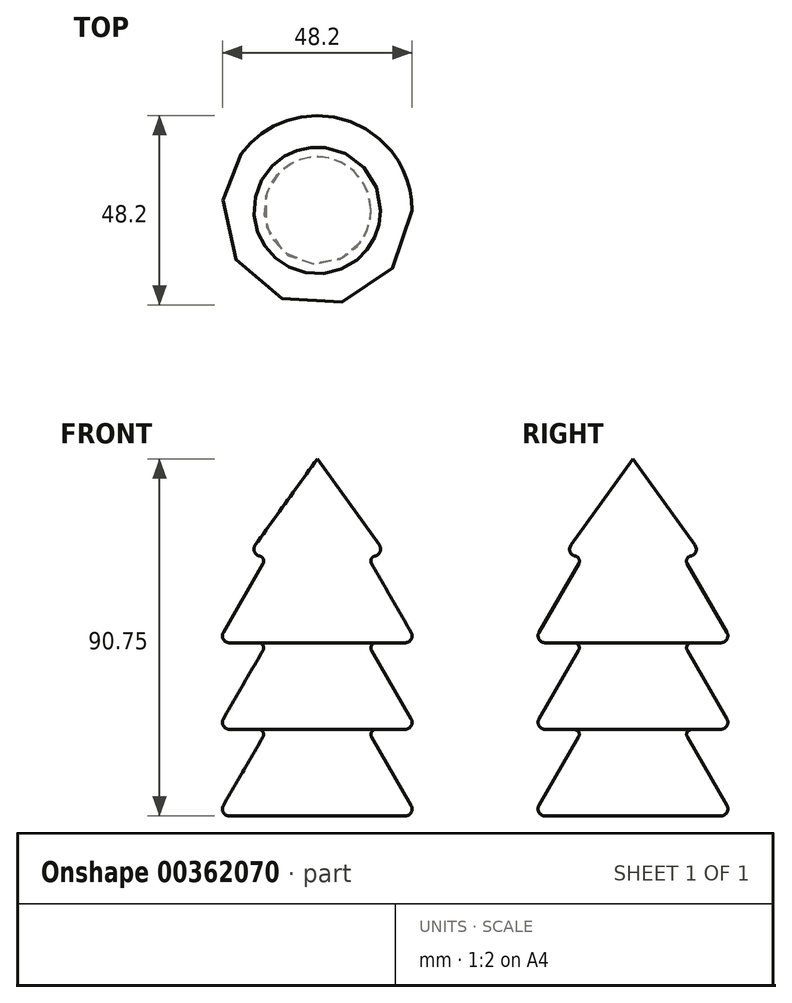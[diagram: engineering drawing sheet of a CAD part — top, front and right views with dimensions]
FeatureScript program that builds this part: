
annotation { "Feature Type Name" : "Feature", "Feature Type Description" : "" }
export const myFeature = defineFeature(function(context is Context, id is Id, definition is map)
    precondition{}
    {
        {
            var Q0;
            Q0=qCreatedBy(makeId("Front.planeOp"),FACE);
            var sketch = newSketch(context, id + "F0", { "sketchPlane" : qUnion([Q0])});
            skLineSegment(sketch, "E0", {"start": v(0, -34.34) * mm, "end": v(-25.4, -34.34) * mm});
            skLineSegment(sketch, "E1", {"start": v(-25.4, -34.34) * mm, "end": v(-12.7, -12.34) * mm});
            skLineSegment(sketch, "E2", {"start": v(-12.7, -12.34) * mm, "end": v(-25.4, -12.34) * mm});
            skLineSegment(sketch, "E3", {"start": v(-25.4, -12.34) * mm, "end": v(-12.7, 9.65) * mm});
            skLineSegment(sketch, "E4", {"start": v(-12.7, 9.65) * mm, "end": v(-25.4, 9.65) * mm});
            skLineSegment(sketch, "E5", {"start": v(-25.4, 9.65) * mm, "end": v(-12.7, 31.65) * mm});
            skLineSegment(sketch, "E6", {"start": v(-12.7, 31.65) * mm, "end": v(-17.78, 31.65) * mm});
            skLineSegment(sketch, "E7", {"start": v(-17.78, 31.65) * mm, "end": v(0, 56.4) * mm});
            skLineSegment(sketch, "E8", {"start": v(0, 56.4) * mm, "end": v(0, -34.34) * mm});
            skSolve(sketch);
        }
        {
            var Q0;
            Q0=makeQuery(id+"F0.imprint","IMPRINT",FACE,{"disambiguationData":[TD([[makeQuery(id+"F0.imprint","IMPRINT",EDGE,{"derivedFrom":sQuery(id+"F0.wireOp",EDGE,"E0")}),-1.0]])]});
            var Q1;
            Q1=sQuery(id+"F0.wireOp",EDGE,"E8");
            revolve(context, id + "F1", {"entities" : qUnion([Q0]), "axis" : qUnion([Q1]), "revolveType" : RevolveType.FULL});
        }
        {
            var Q0;
            Q0=makeQuery(id+"F1.opRevolve","SWEPT_EDGE",EDGE,{"disambiguationData":[OSD([sQuery(id+"F0.wireOp",EDGE,"E6"),sQuery(id+"F0.wireOp",EDGE,"E7")])]});
            var Q1;
            Q1=makeQuery(id+"F1.opRevolve","SWEPT_EDGE",EDGE,{"disambiguationData":[OSD([sQuery(id+"F0.wireOp",EDGE,"E4"),sQuery(id+"F0.wireOp",EDGE,"E5")])]});
            var Q2;
            Q2=makeQuery(id+"F1.opRevolve","SWEPT_EDGE",EDGE,{"disambiguationData":[OSD([sQuery(id+"F0.wireOp",EDGE,"E2"),sQuery(id+"F0.wireOp",EDGE,"E3")])]});
            var Q3;
            Q3=makeQuery(id+"F1.opRevolve","SWEPT_EDGE",EDGE,{"disambiguationData":[OSD([sQuery(id+"F0.wireOp",EDGE,"E0"),sQuery(id+"F0.wireOp",EDGE,"E1")])]});
            var Q4;
            Q4=makeQuery(id+"F1.opRevolve","SWEPT_EDGE",EDGE,{"disambiguationData":[OSD([sQuery(id+"F0.wireOp",EDGE,"PEDuSIMA-l5g4-HbAT-GKb6-t3eDujLnDLOg"),sQuery(id+"F0.wireOp",EDGE,"pMVahdCs-jpBn-ICkF-2S0o-KDSO02qfkrDs")])]});
            fillet(context, id + "F2", {"entities" : qUnion([Q0, Q1, Q2, Q3, Q4]), "radius" : 1.78 * mm, "tangentPropagation" : true, "allowEdgeOverflow" : false});
        }
        {
            var Q0;
            Q0=makeQuery(id+"F1.opRevolve","SWEPT_EDGE",EDGE,{"disambiguationData":[OSD([sQuery(id+"F0.wireOp",EDGE,"E5"),sQuery(id+"F0.wireOp",EDGE,"E6")])]});
            var Q1;
            Q1=makeQuery(id+"F1.opRevolve","SWEPT_EDGE",EDGE,{"disambiguationData":[OSD([sQuery(id+"F0.wireOp",EDGE,"pMVahdCs-jpBn-ICkF-2S0o-KDSO02qfkrDs"),sQuery(id+"F0.wireOp",EDGE,"E0")])]});
            var Q2;
            Q2=makeQuery(id+"F1.opRevolve","SWEPT_EDGE",EDGE,{"disambiguationData":[OSD([sQuery(id+"F0.wireOp",EDGE,"E1"),sQuery(id+"F0.wireOp",EDGE,"E2")])]});
            var Q3;
            Q3=makeQuery(id+"F1.opRevolve","SWEPT_EDGE",EDGE,{"disambiguationData":[OSD([sQuery(id+"F0.wireOp",EDGE,"E3"),sQuery(id+"F0.wireOp",EDGE,"E4")])]});
            fillet(context, id + "F3", {"entities" : qUnion([Q0, Q1, Q2, Q3]), "radius" : 1.27 * mm, "tangentPropagation" : true, "allowEdgeOverflow" : false});
        }
    });
